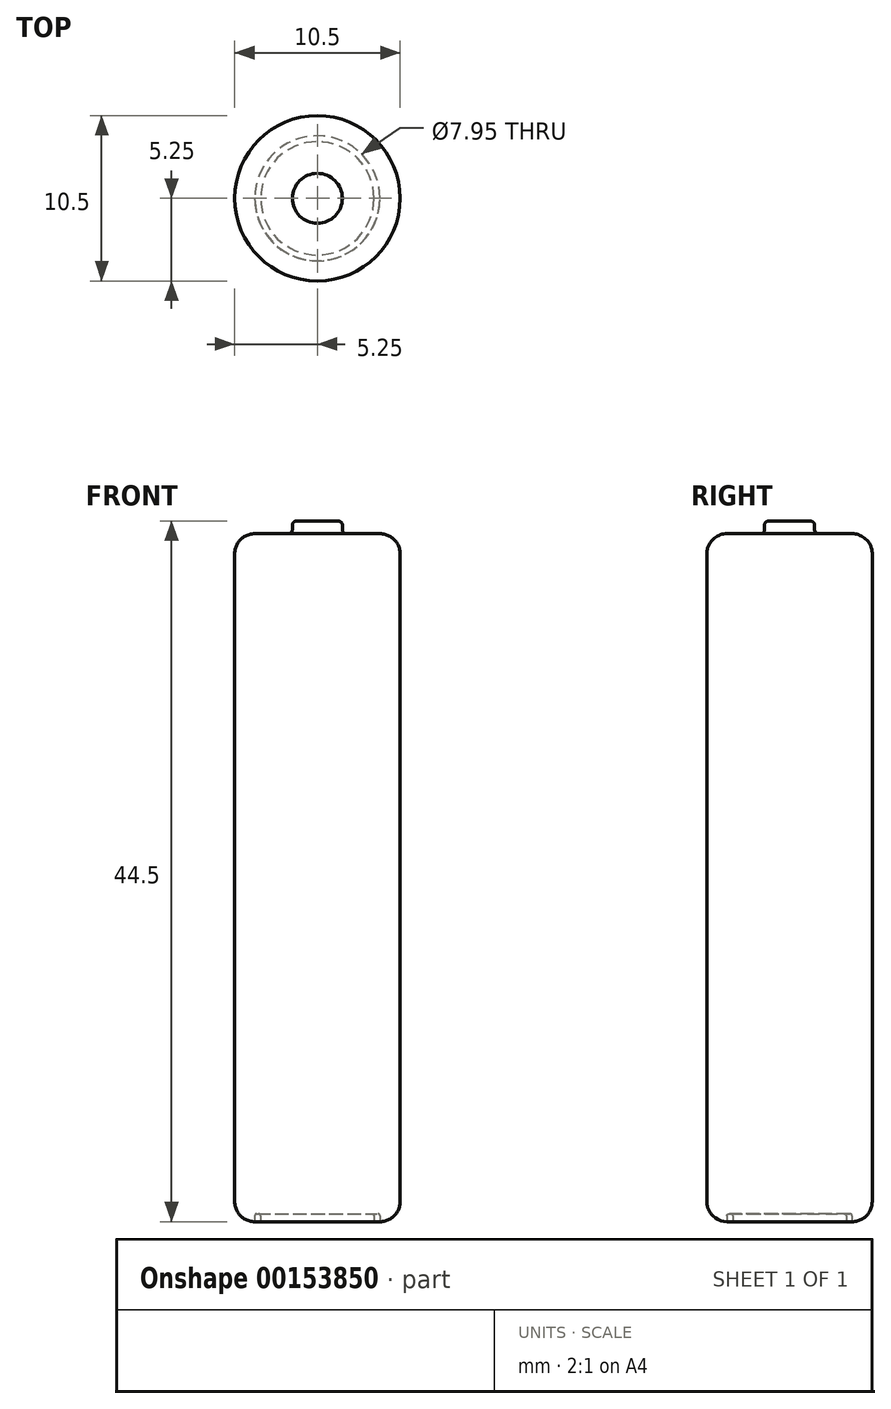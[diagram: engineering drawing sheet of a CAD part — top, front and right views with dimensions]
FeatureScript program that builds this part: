
annotation { "Feature Type Name" : "Feature", "Feature Type Description" : "" }
export const myFeature = defineFeature(function(context is Context, id is Id, definition is map)
    precondition{}
    {
        {
            var Q0;
            Q0=qCreatedBy(makeId("Top.planeOp"),FACE);
            var sketch = newSketch(context, id + "F0", { "sketchPlane" : qUnion([Q0])});
            skCircle(sketch, "E0", {"center": v(0, 0) * mm, "radius": 5.25 * mm});
            skSolve(sketch);
        }
        {
            var Q0;
            Q0 = qSketchRegion(id + "F0", true);
            extrude(context, id + "F1", {"entities" : qUnion([Q0]), "depth" : 43.7 * mm});
        }
        {
            var Q0;
            Q0=makeQuery(id+"F1.opExtrude","CAP_FACE",FACE,{"disambiguationData":[OSD([sQuery(id+"F0.wireOp",EDGE,"E0")])],"isStart":false});
            var sketch = newSketch(context, id + "F2", { "sketchPlane" : qUnion([Q0])});
            skCircle(sketch, "E1", {"center": v(0, 0) * mm, "radius": 1.59 * mm});
            skSolve(sketch);
        }
        {
            var Q0;
            Q0 = qSketchRegion(id + "F2", true);
            extrude(context, id + "F3", {"entities" : qUnion([Q0]), "operationType" : NewBodyOperationType.ADD, "depth" : .8 * mm});
        }
        {
            var Q0;
            Q0=makeQuery(id+"F1.opExtrude","CAP_EDGE",EDGE,{"disambiguationData":[OSD([sQuery(id+"F0.wireOp",EDGE,"E0")])],"isStart":false});
            var Q1;
            Q1=makeQuery(id+"F1.opExtrude","CAP_EDGE",EDGE,{"disambiguationData":[OSD([sQuery(id+"F0.wireOp",EDGE,"E0")])],"isStart":true});
            fillet(context, id + "F4", {"entities" : qUnion([Q0, Q1]), "radius" : 1.27 * mm, "tangentPropagation" : true, "allowEdgeOverflow" : false});
        }
        {
            var Q0;
            Q0=makeQuery(id+"F3.opExtrude","CAP_FACE",FACE,{"disambiguationData":[OSD([sQuery(id+"F2.wireOp",EDGE,"E1")])],"isStart":false});
            var Q1;
            Q1=makeQuery(id+"F1.opExtrude","CAP_FACE",FACE,{"disambiguationData":[OSD([sQuery(id+"F0.wireOp",EDGE,"E0")])],"isStart":false});
            fillet(context, id + "F5", {"entities" : qUnion([Q0, Q1]), "radius" : 0.25 * mm, "tangentPropagation" : true, "allowEdgeOverflow" : false});
        }
        {
            var Q0;
            Q0=makeQuery(id+"F1.opExtrude","CAP_FACE",FACE,{"disambiguationData":[OSD([sQuery(id+"F0.wireOp",EDGE,"E0")])],"isStart":true});
            var sketch = newSketch(context, id + "F6", { "sketchPlane" : qUnion([Q0])});
            skCircle(sketch, "E2", {"center": v(0, 0) * mm, "radius": 3.98 * mm});
            skCircle(sketch, "E3", {"center": v(0, 0) * mm, "radius": 3.6 * mm});
            skSolve(sketch);
        }
        {
            var Q0;
            Q0 = qSketchRegion(id + "F6", true);
            extrude(context, id + "F7", {"entities" : qUnion([Q0]), "operationType" : NewBodyOperationType.REMOVE, "oppositeDirection" : true, "depth" : .5 * mm});
        }
        {
            var Q0;
            Q0=makeQuery(id+"F7.boolean.opBoolean","COPY",FACE,{"derivedFrom":makeQuery(id+"F7.opExtrude","CAP_FACE",FACE,{"disambiguationData":[OSD([sQuery(id+"F6.wireOp",EDGE,"E2"),sQuery(id+"F6.wireOp",EDGE,"E3")])],"isStart":false})});
            var Q1;
            Q1=makeQuery(id+"F7.boolean.opBoolean","COPY",EDGE,{"derivedFrom":makeQuery(id+"F7.opExtrude","CAP_EDGE",EDGE,{"disambiguationData":[OSD([sQuery(id+"F6.wireOp",EDGE,"E3")])],"isStart":true})});
            fillet(context, id + "F8", {"entities" : qUnion([Q0, Q1]), "radius" : 0.13 * mm, "tangentPropagation" : true, "allowEdgeOverflow" : false});
        }
    });
